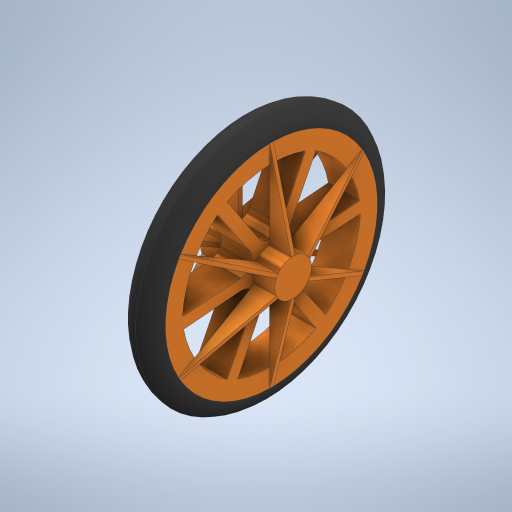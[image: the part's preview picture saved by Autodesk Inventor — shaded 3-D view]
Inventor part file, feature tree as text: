
AUTODESK INVENTOR PART (.ipt)
format: ipt  version: 2023 (Build 270158000, 158)  size: 512,000 bytes
history: native  units: in
note: dims shown in document units (in); Inventor stores cm internally (conversion verified against a paired STEP export)
features: extrude x4, sketch x4, pattern_circular x2, fillet x2, mirror x1, plane x1
ambient origin geometry x8: Origin, YZ Plane, XZ Plane, XY Plane, X Axis, Y Axis, Z Axis, Center Point
bodies: Solid1 (feature_tree)
feature tree (14):
  extrude  "Extrusion1"  Depth=0.9843in
  extrude  "Extrusion2"  Depth=0.689in TaperAngle=0.0deg
  extrude  "Extrusion3"  Depth=3.1496in
  pattern_circular  "Circular Pattern1"  [2 undecoded]
  fillet  "Fillet1"  Radius=3.1496in
  fillet  "Fillet2"  Radius=0.9843in
  extrude  "Extrusion4"  Depth=2.3622in TaperAngle=360.0deg
  pattern_circular  "Circular Pattern2"  [2 undecoded]
  mirror  "Mirror1"
  sketch  "Sketch1"  dims[d0=0.9843in d1=0.0in d2=7.874in]
  sketch  "Sketch2"  dims[d3=1.1811in d4=0.689in d5=1.6732in d6=0.0in d7=0.0in]
  sketch  "Sketch3"  dims[d8=3.1496in d10=3.1496in]
  sketch  "Sketch4"  dims[d12=60.0deg d14=0.3937in d15=3.1496in d16=0.9843in d17=0.0in d18=2.3622in d19=360.0deg d21=0.5906in d22=0.5906in d23=0.1181in d24=0.0in d25=2.3622in d26=360.0deg]
  plane  "Work Plane1"
note: 4 required parameter values undecoded (feature->parameter linkage not recoverable at this tier; creation-order binding heuristic only, values carry confidence <= 0.55)
